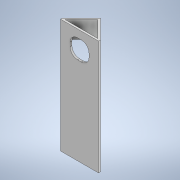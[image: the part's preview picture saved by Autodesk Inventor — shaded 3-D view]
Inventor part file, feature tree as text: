
AUTODESK INVENTOR PART (.ipt)
format: ipt  version: 2020 (Build 240168000, 168)  size: 140,800 bytes
history: native  units: mm
features: extrude x3, sketch x3
ambient origin geometry x8: Origin, YZ Plane, XZ Plane, XY Plane, X Axis, Y Axis, Z Axis, Center Point
bodies: Solid1 (feature_tree)
feature tree (6):
  extrude  "Extrusion1"  Depth=300.0mm
  extrude  "Extrusion2"  TaperAngle=45.0deg  [1 undecoded]
  extrude  "Extrusion6"  Depth=5.0mm
  sketch  "Sketch1"  dims[d0=100.0mm d1=300.0mm]
  sketch  "Sketch2"  dims[d2=5.0mm d3=0.0mm d4=45.0deg]
  sketch  "Sketch6"  dims[d5=5.0mm d6=5.0mm d7=45.0mm d8=0.0mm d21=50.0mm d22=50.0mm d23=20.0mm d24=5.0mm d25=0.0mm]
note: 1 required parameter value undecoded (feature->parameter linkage not recoverable at this tier; creation-order binding heuristic only, values carry confidence <= 0.55)
